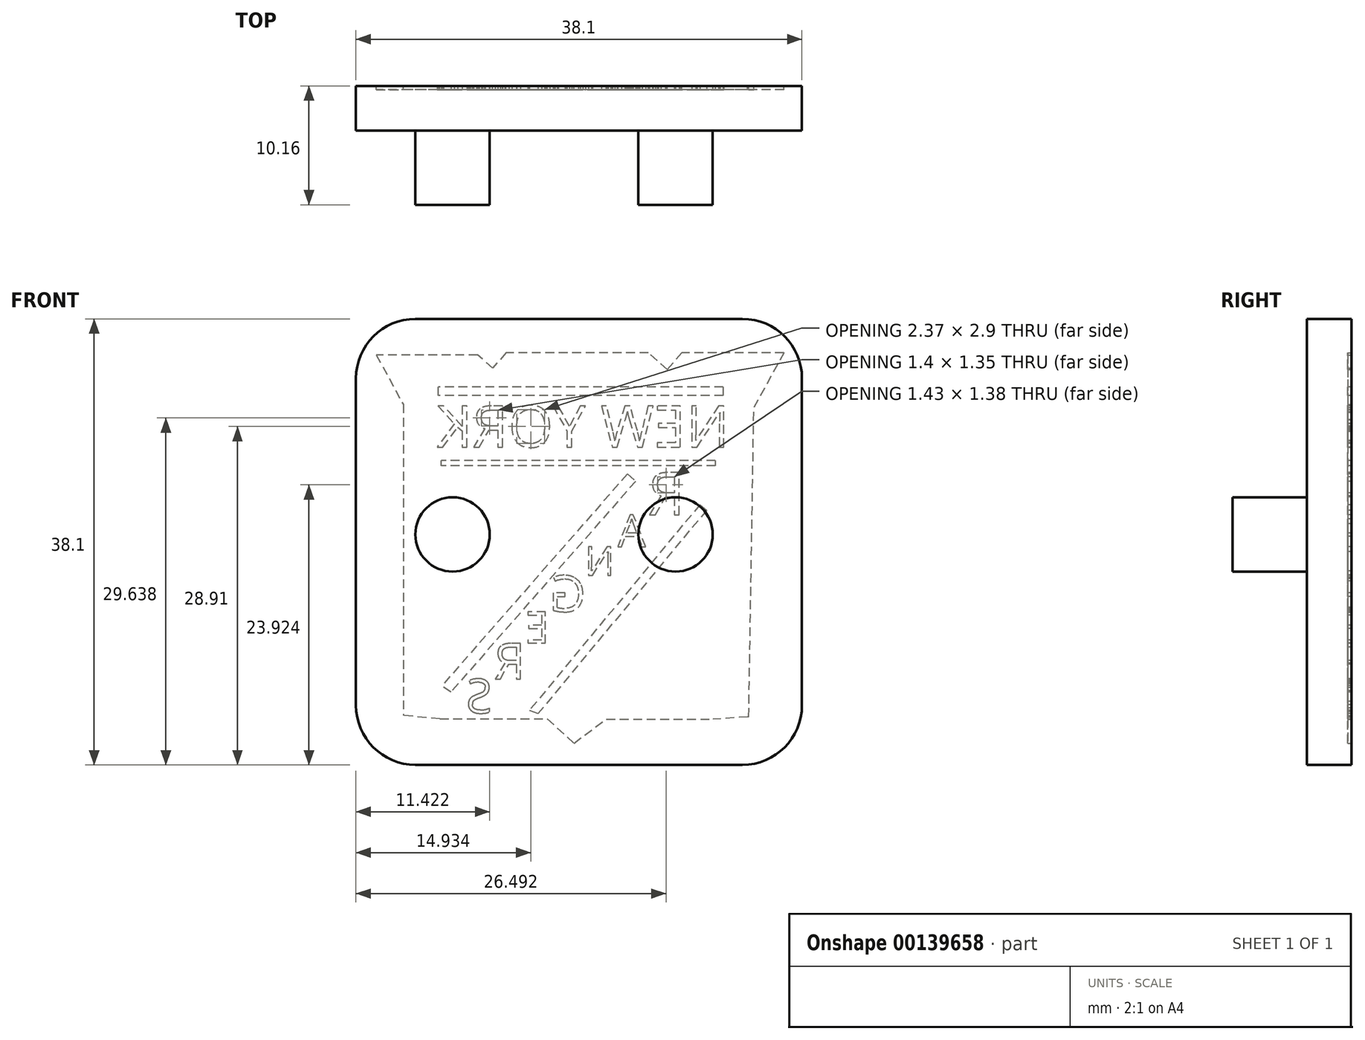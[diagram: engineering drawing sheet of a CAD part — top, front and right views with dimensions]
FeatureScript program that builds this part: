
annotation { "Feature Type Name" : "Feature", "Feature Type Description" : "" }
export const myFeature = defineFeature(function(context is Context, id is Id, definition is map)
    precondition{}
    {
        {
            var Q0;
            Q0=qCreatedBy(makeId("Front.planeOp"),FACE);
            cPlane(context, id + "F0", {"entities" : qUnion([Q0]), "cplaneType" : CPlaneType.OFFSET, "offset" : 25.4 * mm, "width" : 152.4 * mm, "height" : 152.4 * mm});
        }
        {
            var Q0;
            Q0=qCreatedBy(id+"F0.planeOp",FACE);
            var sketch = newSketch(context, id + "F1", { "sketchPlane" : qUnion([Q0])});
            skLineSegment(sketch, "E0.bottom", {"start": v(-40.48, 37.6) * mm, "end": v(-2.38, 37.6) * mm});
            skLineSegment(sketch, "E0.top", {"start": v(-40.48, -0.5) * mm, "end": v(-2.38, -0.5) * mm});
            skLineSegment(sketch, "E0.left", {"start": v(-40.48, 37.6) * mm, "end": v(-40.48, -0.5) * mm});
            skLineSegment(sketch, "E0.right", {"start": v(-2.38, 37.6) * mm, "end": v(-2.38, -0.5) * mm});
            skSolve(sketch);
        }
        {
            var Q0;
            Q0=makeQuery(id+"F1.imprint","IMPRINT",FACE,{"disambiguationData":[TD([[makeQuery(id+"F1.imprint","IMPRINT",EDGE,{"derivedFrom":sQuery(id+"F1.wireOp",EDGE,"E0.bottom")}),-1.0]])]});
            extrude(context, id + "F2", {"entities" : qUnion([Q0]), "depth" : 3.8 * mm});
        }
        {
            var Q0;
            Q0=makeQuery(id+"F2.opExtrude","CAP_FACE",FACE,{"disambiguationData":[OSD([sQuery(id+"F1.wireOp",EDGE,"E0.bottom"),sQuery(id+"F1.wireOp",EDGE,"E0.top"),sQuery(id+"F1.wireOp",EDGE,"E0.left"),sQuery(id+"F1.wireOp",EDGE,"E0.right")])],"isStart":false});
            var sketch = newSketch(context, id + "F3", { "sketchPlane" : qUnion([Q0])});
            skCircle(sketch, "E1", {"center": v(-32.22, 19.19) * mm, "radius": 3.18 * mm});
            skCircle(sketch, "E2", {"center": v(-13.17, 19.19) * mm, "radius": 3.18 * mm});
            skSolve(sketch);
        }
        {
            var Q0;
            Q0=qSketchRegion(id+"F3",true);
            extrude(context, id + "F4", {"entities" : qUnion([Q0]), "operationType" : NewBodyOperationType.ADD, "depth" : 6.35 * mm});
        }
        {
            var Q0;
            Q0=makeQuery(id+"F2.opExtrude","SWEPT_EDGE",EDGE,{"disambiguationData":[OSD([sQuery(id+"F1.wireOp",EDGE,"E0.bottom"),sQuery(id+"F1.wireOp",EDGE,"E0.left")])]});
            var Q1;
            Q1=makeQuery(id+"F2.opExtrude","SWEPT_EDGE",EDGE,{"disambiguationData":[OSD([sQuery(id+"F1.wireOp",EDGE,"E0.bottom"),sQuery(id+"F1.wireOp",EDGE,"E0.right")])]});
            var Q2;
            Q2=makeQuery(id+"F2.opExtrude","SWEPT_EDGE",EDGE,{"disambiguationData":[OSD([sQuery(id+"F1.wireOp",EDGE,"E0.top"),sQuery(id+"F1.wireOp",EDGE,"E0.left")])]});
            var Q3;
            Q3=makeQuery(id+"F2.opExtrude","SWEPT_EDGE",EDGE,{"disambiguationData":[OSD([sQuery(id+"F1.wireOp",EDGE,"E0.top"),sQuery(id+"F1.wireOp",EDGE,"E0.right")])]});
            fillet(context, id + "F5", {"entities" : qUnion([Q0, Q1, Q2, Q3]), "radius" : 5.08 * mm, "tangentPropagation" : true, "allowEdgeOverflow" : false});
        }
        {
            var Q0;
            Q0=makeQuery(id+"F2.opExtrude","CAP_FACE",FACE,{"disambiguationData":[OSD([sQuery(id+"F1.wireOp",EDGE,"E0.bottom"),sQuery(id+"F1.wireOp",EDGE,"E0.top"),sQuery(id+"F1.wireOp",EDGE,"E0.left"),sQuery(id+"F1.wireOp",EDGE,"E0.right")])],"isStart":true});
            var sketch = newSketch(context, id + "F6", { "sketchPlane" : qUnion([Q0])});
            skPoint(sketch, "E3.secondSnap0", {"position": v(38.99, 1) * mm});
            skSolve(sketch);
        }
        {
            var Q0;
            {var subQ3=sQuery(id+"F1.wireOp",EDGE,"E0.bottom");Q0=makeQuery(id+"F6.imprint","IMPRINT",FACE,{"disambiguationData":[TD([[makeQuery(id+"F6.imprint","IMPRINT",EDGE,{"derivedFrom":makeQuery(id+"F2.opExtrude","CAP_EDGE",EDGE,{"disambiguationData":[OSD([subQ3])],"isStart":true})}),1.0]])]});}
            var sketch = newSketch(context, id + "F7", { "sketchPlane" : qUnion([Q0])});
            skLineSegment(sketch, "E4", {"start": v(3.91, 34.72) * mm, "end": v(6.49, 30.03) * mm});
            skLineSegment(sketch, "E5", {"start": v(3.91, 34.72) * mm, "end": v(12.63, 34.72) * mm});
            skLineSegment(sketch, "E6", {"start": v(12.63, 34.72) * mm, "end": v(13.88, 33.3) * mm});
            skLineSegment(sketch, "E7", {"start": v(13.88, 33.3) * mm, "end": v(15.5, 34.7) * mm});
            skLineSegment(sketch, "E8", {"start": v(15.5, 34.7) * mm, "end": v(27.65, 34.7) * mm});
            skLineSegment(sketch, "E9", {"start": v(27.65, 34.7) * mm, "end": v(28.8, 33.4) * mm});
            skLineSegment(sketch, "E10", {"start": v(28.8, 33.4) * mm, "end": v(30.09, 34.53) * mm});
            skLineSegment(sketch, "E11", {"start": v(30.4, 34.53) * mm, "end": v(38.73, 34.53) * mm});
            skLineSegment(sketch, "E12", {"start": v(38.73, 34.53) * mm, "end": v(36.44, 30.3) * mm});
            skLineSegment(sketch, "E13", {"start": v(36.44, 30.3) * mm, "end": v(36.44, 6.67) * mm});
            skLineSegment(sketch, "E14", {"start": v(33.31, 3.42) * mm, "end": v(24.12, 3.42) * mm});
            skLineSegment(sketch, "E15", {"start": v(24.12, 3.42) * mm, "end": v(21.85, 1.35) * mm});
            skLineSegment(sketch, "E16", {"start": v(21.85, 1.35) * mm, "end": v(19.09, 3.4) * mm});
            skLineSegment(sketch, "E17", {"start": v(19.09, 3.4) * mm, "end": v(9.97, 3.4) * mm});
            skLineSegment(sketch, "E18", {"start": v(6.88, 5.98) * mm, "end": v(6.49, 30.03) * mm});
            skLineSegment(sketch, "E19", {"start": v(36.44, 6.67) * mm, "end": v(36.44, 3.72) * mm});
            skLineSegment(sketch, "E20", {"start": v(33.31, 3.42) * mm, "end": v(36.44, 3.72) * mm});
            skLineSegment(sketch, "E21", {"start": v(6.88, 5.98) * mm, "end": v(6.92, 3.6) * mm});
            skLineSegment(sketch, "E22", {"start": v(7, 3.6) * mm, "end": v(9.97, 3.4) * mm});
            skLineSegment(sketch, "E23", {"start": v(6.92, 3.6) * mm, "end": v(7, 3.6) * mm});
            skLineSegment(sketch, "E24", {"start": v(30.4, 34.53) * mm, "end": v(30.09, 34.53) * mm});
            skSolve(sketch);
        }
        {
            var Q0;
            Q0=qSketchRegion(id+"F7",true);
            extrude(context, id + "F8", {"entities" : qUnion([Q0]), "operationType" : NewBodyOperationType.REMOVE, "oppositeDirection" : true, "depth" : 0.32 * mm});
        }
        {
            var Q0;
            Q0=makeQuery(id+"F8.boolean.opBoolean","COPY",FACE,{"derivedFrom":makeQuery(id+"F8.opExtrude","CAP_FACE",FACE,{"disambiguationData":[OSD([sQuery(id+"F7.wireOp",EDGE,"E4"),sQuery(id+"F7.wireOp",EDGE,"E5"),sQuery(id+"F7.wireOp",EDGE,"E6"),sQuery(id+"F7.wireOp",EDGE,"E7"),sQuery(id+"F7.wireOp",EDGE,"E8"),sQuery(id+"F7.wireOp",EDGE,"E9"),sQuery(id+"F7.wireOp",EDGE,"E10"),sQuery(id+"F7.wireOp",EDGE,"E11"),sQuery(id+"F7.wireOp",EDGE,"E12"),sQuery(id+"F7.wireOp",EDGE,"E13"),sQuery(id+"F7.wireOp",EDGE,"E14"),sQuery(id+"F7.wireOp",EDGE,"E15"),sQuery(id+"F7.wireOp",EDGE,"E16"),sQuery(id+"F7.wireOp",EDGE,"E17"),sQuery(id+"F7.wireOp",EDGE,"E18"),sQuery(id+"F7.wireOp",EDGE,"E19"),sQuery(id+"F7.wireOp",EDGE,"E20"),sQuery(id+"F7.wireOp",EDGE,"E21"),sQuery(id+"F7.wireOp",EDGE,"E22"),sQuery(id+"F7.wireOp",EDGE,"E23"),sQuery(id+"F7.wireOp",EDGE,"E24")])],"isStart":false})});
            var sketch = newSketch(context, id + "F9", { "sketchPlane" : qUnion([Q0])});
            skText(sketch, "E25", { "text": "NEW YORK", "fontName": "OpenSans-Regular.ttf"});
            skText(sketch, "E26", { "text": "R", "fontName": "OpenSans-Regular.ttf"});
            skText(sketch, "E27", { "text": "A", "fontName": "OpenSans-Regular.ttf"});
            skText(sketch, "E28", { "text": "N", "fontName": "OpenSans-Regular.ttf"});
            skText(sketch, "E29", { "text": "G", "fontName": "OpenSans-Regular.ttf"});
            skText(sketch, "E30", { "text": "E", "fontName": "OpenSans-Regular.ttf"});
            skText(sketch, "E31", { "text": "R", "fontName": "OpenSans-Regular.ttf"});
            skText(sketch, "E32", { "text": "S", "fontName": "OpenSans-Regular.ttf"});
            const initialGuessF9  = {"E25": [0.00856, 0.02665, 1, 0, 0.00355], "E26": [0.01236, 0.02088, 1, 0, 0.00363], "E27": [0.01572, 0.01815, 1, 0, 0.00273], "E28": [0.01836, 0.01568, 1, 0, 0.00246], "E29": [0.02083, 0.0126, 1, 0, 0.00309], "E30": [0.02392, 0.0099, 1, 0, 0.0027], "E31": [0.02601, 0.00684, 1, 0, 0.00306], "E32": [0.02884, 0.00393, 1, 0, 0.00292]};
            skSetInitialGuess(sketch, initialGuessF9);
            skSolve(sketch);
        }
        {
            var Q0;
            Q0=qSketchRegion(id+"F9",true);
            extrude(context, id + "F10", {"entities" : qUnion([Q0]), "depth" : 0.32 * mm});
        }
        {
            var Q0;
            Q0=makeQuery(id+"F8.boolean.opBoolean","COPY",FACE,{"derivedFrom":makeQuery(id+"F8.opExtrude","CAP_FACE",FACE,{"disambiguationData":[OSD([sQuery(id+"F7.wireOp",EDGE,"E4"),sQuery(id+"F7.wireOp",EDGE,"E5"),sQuery(id+"F7.wireOp",EDGE,"E6"),sQuery(id+"F7.wireOp",EDGE,"E7"),sQuery(id+"F7.wireOp",EDGE,"E8"),sQuery(id+"F7.wireOp",EDGE,"E9"),sQuery(id+"F7.wireOp",EDGE,"E10"),sQuery(id+"F7.wireOp",EDGE,"E11"),sQuery(id+"F7.wireOp",EDGE,"E12"),sQuery(id+"F7.wireOp",EDGE,"E13"),sQuery(id+"F7.wireOp",EDGE,"E14"),sQuery(id+"F7.wireOp",EDGE,"E15"),sQuery(id+"F7.wireOp",EDGE,"E16"),sQuery(id+"F7.wireOp",EDGE,"E17"),sQuery(id+"F7.wireOp",EDGE,"E18"),sQuery(id+"F7.wireOp",EDGE,"E19"),sQuery(id+"F7.wireOp",EDGE,"E20"),sQuery(id+"F7.wireOp",EDGE,"E21"),sQuery(id+"F7.wireOp",EDGE,"E22"),sQuery(id+"F7.wireOp",EDGE,"E23"),sQuery(id+"F7.wireOp",EDGE,"E24")])],"isStart":false})});
            var sketch = newSketch(context, id + "F11", { "sketchPlane" : qUnion([Q0])});
            skLineSegment(sketch, "E33", {"start": v(9.11, 31.8) * mm, "end": v(33.45, 31.8) * mm});
            skLineSegment(sketch, "E34", {"start": v(9.78, 25.5) * mm, "end": v(33.17, 25.5) * mm});
            skLineSegment(sketch, "E35", {"start": v(17.29, 24.35) * mm, "end": v(33.14, 6.25) * mm});
            skLineSegment(sketch, "E36", {"start": v(11.1, 21.73) * mm, "end": v(25.67, 4.15) * mm});
            skLineSegment(sketch, "E37", {"start": v(9.78, 25.5) * mm, "end": v(9.78, 25.05) * mm});
            skLineSegment(sketch, "E38", {"start": v(9.78, 25.05) * mm, "end": v(33.17, 25.05) * mm});
            skLineSegment(sketch, "E39", {"start": v(33.17, 25.05) * mm, "end": v(33.17, 25.5) * mm});
            skLineSegment(sketch, "E40", {"start": v(9.11, 31.8) * mm, "end": v(9.11, 31.05) * mm});
            skLineSegment(sketch, "E41", {"start": v(9.11, 31.05) * mm, "end": v(33.44, 31.05) * mm});
            skLineSegment(sketch, "E42", {"start": v(33.44, 31.05) * mm, "end": v(33.45, 31.8) * mm});
            skLineSegment(sketch, "E43", {"start": v(11.1, 21.73) * mm, "end": v(10.53, 21.26) * mm});
            skLineSegment(sketch, "E44", {"start": v(10.53, 21.26) * mm, "end": v(24.92, 3.88) * mm});
            skLineSegment(sketch, "E45", {"start": v(24.92, 3.88) * mm, "end": v(25.67, 4.15) * mm});
            skLineSegment(sketch, "E46", {"start": v(17.29, 24.35) * mm, "end": v(16.58, 23.74) * mm});
            skLineSegment(sketch, "E47", {"start": v(16.58, 23.74) * mm, "end": v(32.36, 5.72) * mm});
            skLineSegment(sketch, "E48", {"start": v(32.36, 5.72) * mm, "end": v(33.14, 6.25) * mm});
            skSolve(sketch);
        }
        {
            var Q0;
            Q0=qSketchRegion(id+"F11",true);
            extrude(context, id + "F12", {"entities" : qUnion([Q0]), "operationType" : NewBodyOperationType.ADD, "depth" : 0.32 * mm});
        }
    });
